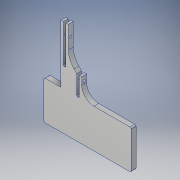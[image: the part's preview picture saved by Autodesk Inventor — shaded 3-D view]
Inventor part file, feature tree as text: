
AUTODESK INVENTOR PART (.ipt)
format: ipt  version: 2017 (Build 210142000, 142)  size: 236,032 bytes
history: native  units: in
note: dims shown in document units (in); Inventor stores cm internally (conversion verified against a paired STEP export)
features: sketch x15, extrude x12, fillet x4
ambient origin geometry x8: Origin, YZ Plane, XZ Plane, XY Plane, X Axis, Y Axis, Z Axis, Center Point
bodies: Solid1 (feature_tree)
feature tree (31):
  extrude  "Extrusion1"  Depth=2.0in
  sketch  "Sketch2"  dims[d3=4.5in d4=0.125in d5=0.0in]
  extrude  "Extrusion2"  Depth=0.125in TaperAngle=0.0deg
  extrude  "Extrusion3"  Depth=0.066in
  extrude  "Extrusion4"  Depth=0.25in
  extrude  "Extrusion5"  Depth=0.125in TaperAngle=0.0deg
  extrude  "Extrusion6"  Depth=3.0in TaperAngle=0.0deg
  sketch  "Sketch6"  dims[d14=3.0in d15=0.0in d16=3.0in d17=0.0in]
  sketch  "Sketch7"  dims[d18=0.75in d19=0.125in]
  sketch  "Sketch8"  dims[d20=2.0in d21=0.0in d22=1.64in]
  sketch  "Sketch9"  dims[d23=0.125in d24=2.0in d25=0.0in]
  extrude  "Extrusion11"  Depth=0.125in
  extrude  "Extrusion12"  Depth=2.0in
  extrude  "Extrusion13"  Depth=2.0in TaperAngle=0.0deg
  extrude  "Extrusion14"  Depth=0.125in
  extrude  "Extrusion15"  Depth=0.125in
  extrude  "Extrusion16"  Depth=0.125in
  fillet  "Fillet1"  Radius=0.25in
  fillet  "Fillet3"  Radius=0.067in
  fillet  "Fillet4"  Radius=0.125in
  fillet  "Fillet5"  Radius=0.25in
  sketch  "Sketch1"  dims[d1=4.5in d2=2.0in]
  sketch  "Sketch3"  dims[d7=0.066in d8=0.066in]
  sketch  "Sketch4"  dims[d9=0.125in d10=0.25in]
  sketch  "Sketch5"  dims[d11=0.125in d12=0.125in d13=0.0in]
  sketch  "Sketch12"  dims[d30=0.125in d34=0.125in]
  sketch  "Sketch13"  dims[d35=0.132in d36=0.125in]
  sketch  "Sketch14"  dims[d44=0.067in d45=0.125in d46=0.25in d47=0.0in d48=0.067in d49=0.125in d50=0.25in d51=0.0in]
  sketch  "Sketch15"  dims[d52=0.125in]
  sketch  "Sketch16"  dims[d55=0.25in d56=0.0in]
  sketch  "Sketch17"  dims[d57=2.0in d58=0.0in d59=0.25in d60=0.0in d61=0.5in d62=0.0in d63=0.0625in d65=1.0in d66=0.0625in d67=0.625in]
